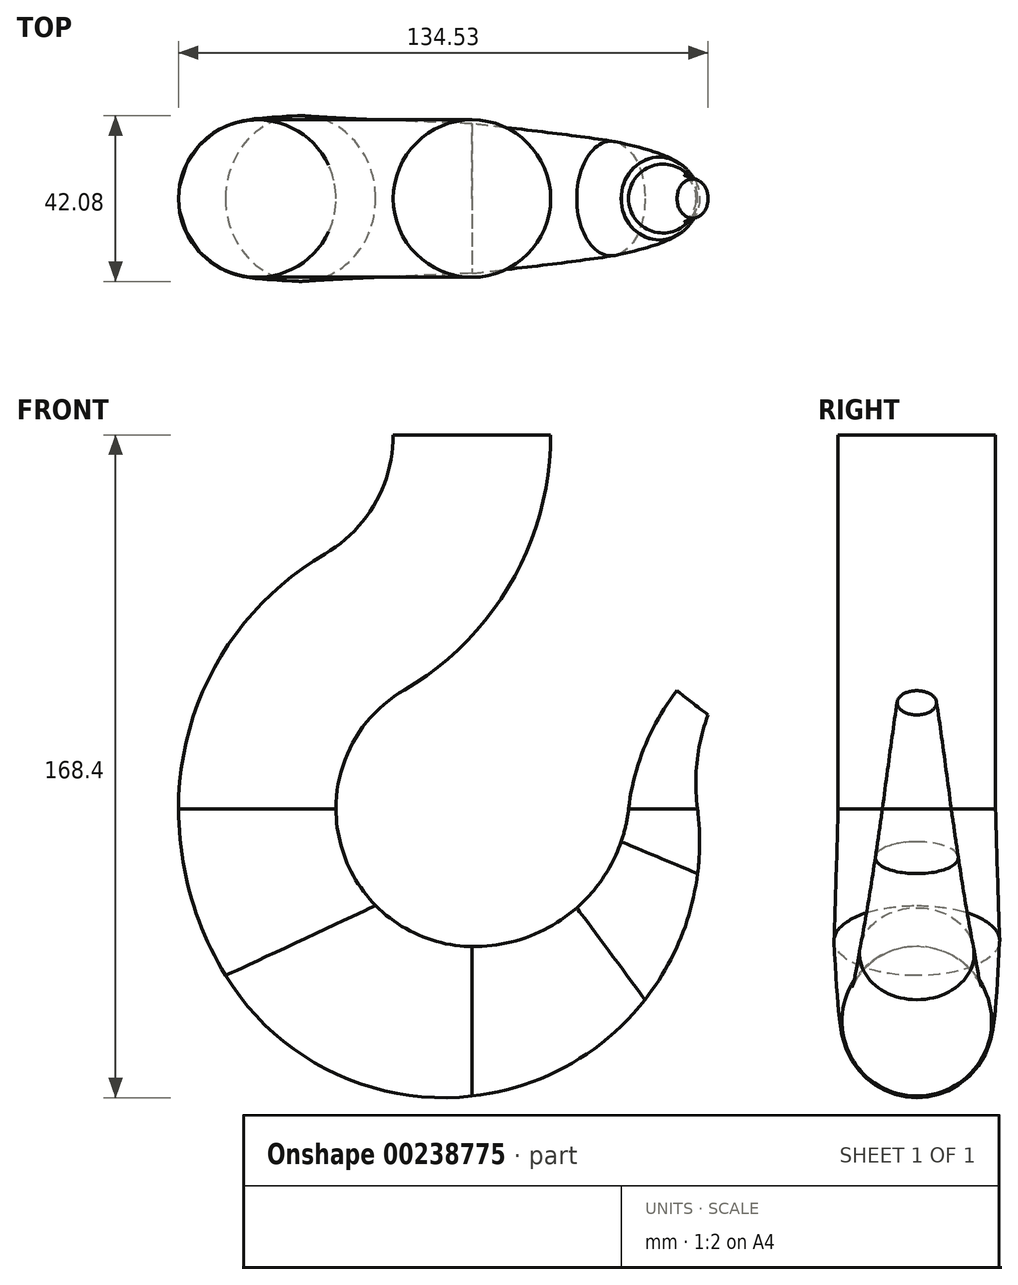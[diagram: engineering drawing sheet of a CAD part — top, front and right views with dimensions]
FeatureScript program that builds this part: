
annotation { "Feature Type Name" : "Feature", "Feature Type Description" : "" }
export const myFeature = defineFeature(function(context is Context, id is Id, definition is map)
    precondition{}
    {
        {
            var Q0;
            Q0=qCreatedBy(makeId("Front.planeOp"),FACE);
            var sketch = newSketch(context, id + "F0", { "sketchPlane" : qUnion([Q0])});
            skLineSegment(sketch, "E0", {"start": v(-107.33, 0) * mm, "end": v(104.55, 0) * mm, "construction": true});
            skLineSegment(sketch, "E1", {"start": v(-0.45, 95.64) * mm, "end": v(-0.45, -96.04) * mm, "construction": true});
            skLineSegment(sketch, "E2", {"start": v(-20.45, 95) * mm, "end": v(19.55, 95) * mm});
            skPoint(sketch, "E3", {"position": v(-0.45, 95) * mm});
            skArc(sketch, "E4", {"start": v(-37.8, 64.77) * mm, "mid": v(-25.1, 77.57) * mm, "end": v(-20.45, 95) * mm});
            skArc(sketch, "E5", {"start": v(-37.8, 64.77) * mm, "mid": v(-65.04, 37.35) * mm, "end": v(-75, 0) * mm});
            skArc(sketch, "E6", {"start": v(-0.45, -73) * mm, "mid": v(43.5, -48.52) * mm, "end": v(56.83, 0) * mm});
            skArc(sketch, "E7", {"start": v(-35, 0) * mm, "mid": v(-24.9, -24.59) * mm, "end": v(-0.45, -35) * mm});
            skArc(sketch, "E8", {"start": v(19.55, 95) * mm, "mid": v(9.59, 57.65) * mm, "end": v(-17.64, 30.23) * mm});
            skArc(sketch, "E9", {"start": v(-35, 0) * mm, "mid": v(-30.35, 17.43) * mm, "end": v(-17.64, 30.23) * mm});
            skArc(sketch, "E10", {"start": v(-0.45, -35) * mm, "mid": v(26.18, -25.15) * mm, "end": v(39.35, 0) * mm});
            skLineSegment(sketch, "E11", {"start": v(32.25, 30) * mm, "end": v(90.74, 30) * mm, "construction": true});
            skPoint(sketch, "E12", {"position": v(67.18, 30) * mm});
            skLineSegment(sketch, "E13", {"start": v(47.43, 30) * mm, "end": v(67.18, 30) * mm});
            skArc(sketch, "E14", {"start": v(-75, 0) * mm, "mid": v(-71.95, -22.02) * mm, "end": v(-63.04, -42.38) * mm});
            skArc(sketch, "E15", {"start": v(39.35, 0) * mm, "mid": v(43.43, 15.85) * mm, "end": v(51.64, 30) * mm});
            skLineSegment(sketch, "E16", {"start": v(51.64, 30) * mm, "end": v(59.53, 23.85) * mm});
            skCircle(sketch, "E17", {"center": v(55.59, 26.92) * mm, "radius": 5 * mm, "construction": true});
            skArc(sketch, "E18", {"start": v(56.83, 0) * mm, "mid": v(56.72, 12.09) * mm, "end": v(59.53, 23.85) * mm});
            skArc(sketch, "E19", {"start": v(-63.04, -42.38) * mm, "mid": v(-36.2, -66.78) * mm, "end": v(-0.45, -73) * mm});
            skLineSegment(sketch, "E20", {"start": v(-37.8, 64.77) * mm, "end": v(-17.64, 30.23) * mm});
            skLineSegment(sketch, "E21", {"start": v(-75, 0) * mm, "end": v(-35, 0) * mm});
            skLineSegment(sketch, "E22", {"start": v(-0.45, -35) * mm, "end": v(-0.45, -73) * mm});
            skLineSegment(sketch, "E23", {"start": v(39.35, 0) * mm, "end": v(56.83, 0) * mm});
            skLineSegment(sketch, "E24", {"start": v(-24.9, -24.59) * mm, "end": v(-63.04, -42.38) * mm});
            skLineSegment(sketch, "E25", {"start": v(26.18, -25.15) * mm, "end": v(43.5, -48.52) * mm});
            skLineSegment(sketch, "E26", {"start": v(37.44, -8.37) * mm, "end": v(56.87, -16.47) * mm});
            skPoint(sketch, "E27", {"position": v(-0.45, 0) * mm});
            skSolve(sketch);
        }
        {
            var Q0;
            Q0=qCreatedBy(makeId("Top.planeOp"),FACE);
            cPlane(context, id + "F1", {"entities" : qUnion([Q0]), "cplaneType" : CPlaneType.OFFSET, "offset" : 95 * mm, "width" : 150 * mm, "height" : 150 * mm});
        }
        {
            var Q0;
            Q0=qCreatedBy(id+"F1.planeOp",FACE);
            var sketch = newSketch(context, id + "F2", { "sketchPlane" : qUnion([Q0])});
            skPoint(sketch, "E28.0", {"position": v(-20.45, 0) * mm});
            skPoint(sketch, "E29.0", {"position": v(-0.45, 0) * mm});
            skCircle(sketch, "E30", {"center": v(-0.45, 0) * mm, "radius": 20 * mm});
            skSolve(sketch);
        }
        {
            var Q0;
            Q0=sQuery(id+"F0.wireOp",EDGE,"E20");
            cPlane(context, id + "F3", {"entities" : qUnion([Q0]), "cplaneType" : CPlaneType.LINE_ANGLE, "offset" : 25 * mm, "angle" : 0 * degree, "width" : 150 * mm, "height" : 150 * mm});
        }
        {
            var Q0;
            Q0=qCreatedBy(id+"F3.planeOp",FACE);
            var sketch = newSketch(context, id + "F4", { "sketchPlane" : qUnion([Q0])});
            skPoint(sketch, "E31.0", {"position": v(0, 75) * mm});
            skPoint(sketch, "E32.0", {"position": v(0, 55) * mm});
            skCircle(sketch, "E33", {"center": v(0, 55) * mm, "radius": 20 * mm});
            skSolve(sketch);
        }
        {
            var Q0;
            Q0=sQuery(id+"F0.wireOp",EDGE,"E21");
            cPlane(context, id + "F5", {"entities" : qUnion([Q0]), "cplaneType" : CPlaneType.LINE_ANGLE, "offset" : 25 * mm, "angle" : 90 * degree, "width" : 150 * mm, "height" : 150 * mm});
        }
        {
            var Q0;
            Q0=qCreatedBy(id+"F5.planeOp",FACE);
            var sketch = newSketch(context, id + "F6", { "sketchPlane" : qUnion([Q0])});
            skPoint(sketch, "E34.0", {"position": v(-55, 0) * mm});
            skPoint(sketch, "E35.0", {"position": v(-75, 0) * mm});
            skCircle(sketch, "E36", {"center": v(-55, 0) * mm, "radius": 20 * mm});
            skSolve(sketch);
        }
        {
            var Q0;
            Q0=makeQuery(id+"F4.imprint","IMPRINT",FACE,{"disambiguationData":[TD([[makeQuery(id+"F4.imprint","IMPRINT",EDGE,{"derivedFrom":sQuery(id+"F4.wireOp",EDGE,"E33")}),1.0]])]});
            var Q1;
            Q1=makeQuery(id+"F6.imprint","IMPRINT",FACE,{"disambiguationData":[TD([[makeQuery(id+"F6.imprint","IMPRINT",EDGE,{"derivedFrom":sQuery(id+"F6.wireOp",EDGE,"E36")}),1.0]])]});
            var Q2;
            Q2=sQuery(id+"F0.wireOp",EDGE,"E5");
            var Q3;
            Q3=sQuery(id+"F0.wireOp",EDGE,"E9");
            loft(context, id + "F7", {"addGuides" : true, "sheetProfilesArray" : [{ "sheetProfileEntities" : qUnion([Q0]) }, { "sheetProfileEntities" : qUnion([Q1]) }], "guidesArray" : [{ "guideEntities" : qUnion([Q2]), "guideDerivativeType" : LoftGuideDerivativeType.DEFAULT, "guideDerivativeMagnitude" : 1 }, { "guideEntities" : qUnion([Q3]), "guideDerivativeType" : LoftGuideDerivativeType.DEFAULT, "guideDerivativeMagnitude" : 1 }]});
        }
        {
            var Q1;
            Q1=makeQuery(id+"F7.opLoft","CAP_FACE",FACE,{"disambiguationData":[OSD([makeQuery(id+"F4.imprint","IMPRINT",FACE,{"disambiguationData":[TD([[makeQuery(id+"F4.imprint","IMPRINT",EDGE,{"derivedFrom":sQuery(id+"F4.wireOp",EDGE,"E33")}),1.0]])]})])],"isStart":true});
            var Q2;
            Q2=makeQuery(id+"F2.imprint","IMPRINT",FACE,{"disambiguationData":[TD([[makeQuery(id+"F2.imprint","IMPRINT",EDGE,{"derivedFrom":sQuery(id+"F2.wireOp",EDGE,"E30")}),1.0]])]});
            var Q3;
            Q3=sQuery(id+"F0.wireOp",EDGE,"E4");
            var Q4;
            Q4=sQuery(id+"F0.wireOp",EDGE,"E8");
            loft(context, id + "F8", {"operationType" : NewBodyOperationType.ADD, "addGuides" : true, "sheetProfilesArray" : [{ "sheetProfileEntities" : qUnion([Q1]) }, { "sheetProfileEntities" : qUnion([Q2]) }], "guidesArray" : [{ "guideEntities" : qUnion([Q3]), "guideDerivativeType" : LoftGuideDerivativeType.DEFAULT, "guideDerivativeMagnitude" : 1 }, { "guideEntities" : qUnion([Q4]), "guideDerivativeType" : LoftGuideDerivativeType.DEFAULT, "guideDerivativeMagnitude" : 1 }]});
        }
        {
            var Q0;
            Q0=sQuery(id+"F0.wireOp",EDGE,"E23");
            cPlane(context, id + "F9", {"entities" : qUnion([Q0]), "cplaneType" : CPlaneType.LINE_ANGLE, "offset" : 25 * mm, "angle" : 90 * degree, "width" : 150 * mm, "height" : 150 * mm});
        }
        {
            var Q0;
            Q0=qCreatedBy(id+"F9.planeOp",FACE);
            var sketch = newSketch(context, id + "F10", { "sketchPlane" : qUnion([Q0])});
            skPoint(sketch, "E37.0", {"position": v(48.09, 0) * mm});
            skPoint(sketch, "E38.0", {"position": v(56.83, 0) * mm});
            skCircle(sketch, "E39", {"center": v(48.09, 0) * mm, "radius": 8.74 * mm});
            skSolve(sketch);
        }
        {
            var Q0;
            Q0=sQuery(id+"F0.wireOp",EDGE,"E16");
            cPlane(context, id + "F11", {"entities" : qUnion([Q0]), "cplaneType" : CPlaneType.LINE_ANGLE, "offset" : 25 * mm, "angle" : 90 * degree, "width" : 150 * mm, "height" : 150 * mm});
        }
        {
            var Q0;
            Q0=qCreatedBy(id+"F11.planeOp",FACE);
            var sketch = newSketch(context, id + "F12", { "sketchPlane" : qUnion([Q0])});
            skLineSegment(sketch, "E40.0", {"start": v(22.27, 0) * mm, "end": v(32.27, 0) * mm, "construction": true});
            skCircle(sketch, "E41", {"center": v(27.27, 0) * mm, "radius": 5 * mm});
            skSolve(sketch);
        }
        {
            var Q0;
            Q0=makeQuery(id+"F0.imprint","IMPRINT",FACE,{"disambiguationData":[TD([[makeQuery(id+"F0.imprint","IMPRINT",EDGE,{"derivedFrom":sQuery(id+"F0.wireOp",EDGE,"E14")}),1.0]])]});
            var sketch = newSketch(context, id + "F13", { "sketchPlane" : qUnion([Q0])});
            skLineSegment(sketch, "E42.0.0", {"start": v(-63.04, -42.38) * mm, "end": v(-24.9, -24.59) * mm});
            skArc(sketch, "E42.0.1", {"start": v(-24.9, -24.59) * mm, "mid": v(-32.38, -13.29) * mm, "end": v(-35, 0) * mm});
            skLineSegment(sketch, "E42.0.2", {"start": v(-35, 0) * mm, "end": v(-75, 0) * mm});
            skArc(sketch, "E42.0.3", {"start": v(-75, 0) * mm, "mid": v(-71.95, -22.02) * mm, "end": v(-63.04, -42.38) * mm});
            skSolve(sketch);
        }
        {
            var Q0;
            Q0=makeQuery(id+"F0.imprint","IMPRINT",FACE,{"disambiguationData":[TD([[makeQuery(id+"F0.imprint","IMPRINT",EDGE,{"derivedFrom":sQuery(id+"F0.wireOp",EDGE,"E19")}),1.0]])]});
            var sketch = newSketch(context, id + "F14", { "sketchPlane" : qUnion([Q0])});
            skArc(sketch, "E43.0.0", {"start": v(-0.45, -35) * mm, "mid": v(-13.7, -32.2) * mm, "end": v(-24.9, -24.59) * mm});
            skLineSegment(sketch, "E43.0.1", {"start": v(-24.9, -24.59) * mm, "end": v(-63.04, -42.38) * mm});
            skArc(sketch, "E43.0.2", {"start": v(-63.04, -42.38) * mm, "mid": v(-36.2, -66.78) * mm, "end": v(-0.45, -73) * mm});
            skLineSegment(sketch, "E43.0.3", {"start": v(-0.45, -73) * mm, "end": v(-0.45, -35) * mm});
            skSolve(sketch);
        }
        {
            var Q0;
            Q0=sQuery(id+"F14.wireOp",EDGE,"E43.0.1");
            cPlane(context, id + "F15", {"entities" : qUnion([Q0]), "cplaneType" : CPlaneType.LINE_ANGLE, "offset" : 25 * mm, "angle" : 90 * degree, "width" : 150 * mm, "height" : 150 * mm});
        }
        {
            var Q0;
            Q0=qCreatedBy(id+"F15.planeOp",FACE);
            var sketch = newSketch(context, id + "F16", { "sketchPlane" : qUnion([Q0])});
            skPoint(sketch, "E44.0", {"position": v(-54, 0) * mm});
            skPoint(sketch, "E45.0", {"position": v(-75.05, 0) * mm});
            skCircle(sketch, "E46", {"center": v(-54, 0) * mm, "radius": 21.04 * mm});
            skSolve(sketch);
        }
        {
            var Q0;
            Q0=makeQuery(id+"F7.opLoft","CAP_FACE",FACE,{"disambiguationData":[OSD([makeQuery(id+"F6.imprint","IMPRINT",FACE,{"disambiguationData":[TD([[makeQuery(id+"F6.imprint","IMPRINT",EDGE,{"derivedFrom":sQuery(id+"F6.wireOp",EDGE,"E36")}),1.0]])]})])],"isStart":true});
            var Q1;
            Q1=makeQuery(id+"F16.imprint","IMPRINT",FACE,{"disambiguationData":[TD([[makeQuery(id+"F16.imprint","IMPRINT",EDGE,{"derivedFrom":sQuery(id+"F16.wireOp",EDGE,"E46")}),1.0]])]});
            var Q2;
            Q2=sQuery(id+"F13.wireOp",EDGE,"E42.0.3");
            var Q3;
            Q3=sQuery(id+"F13.wireOp",EDGE,"E42.0.1");
            loft(context, id + "F17", {"addGuides" : true, "sheetProfilesArray" : [{ "sheetProfileEntities" : qUnion([Q0]) }, { "sheetProfileEntities" : qUnion([Q1]) }], "guidesArray" : [{ "guideEntities" : qUnion([Q2]), "guideDerivativeType" : LoftGuideDerivativeType.DEFAULT, "guideDerivativeMagnitude" : 1 }, { "guideEntities" : qUnion([Q3]), "guideDerivativeType" : LoftGuideDerivativeType.DEFAULT, "guideDerivativeMagnitude" : 1 }]});
        }
        {
            var Q0;
            Q0=sQuery(id+"F14.wireOp",EDGE,"E43.0.3");
            cPlane(context, id + "F18", {"entities" : qUnion([Q0]), "cplaneType" : CPlaneType.LINE_ANGLE, "offset" : 25 * mm, "angle" : 0 * degree, "width" : 150 * mm, "height" : 150 * mm});
        }
        {
            var Q0;
            Q0=qCreatedBy(id+"F18.planeOp",FACE);
            var sketch = newSketch(context, id + "F19", { "sketchPlane" : qUnion([Q0])});
            skPoint(sketch, "E47.0", {"position": v(0, -73) * mm});
            skPoint(sketch, "E48.0", {"position": v(0, -54) * mm});
            skCircle(sketch, "E49", {"center": v(0, -54) * mm, "radius": 19 * mm});
            skSolve(sketch);
        }
        {
            var Q1;
            Q1=makeQuery(id+"F17.opLoft","CAP_FACE",FACE,{"disambiguationData":[OSD([makeQuery(id+"F16.imprint","IMPRINT",FACE,{"disambiguationData":[TD([[makeQuery(id+"F16.imprint","IMPRINT",EDGE,{"derivedFrom":sQuery(id+"F16.wireOp",EDGE,"E46")}),1.0]])]})])],"isStart":true});
            var Q2;
            Q2=makeQuery(id+"F19.imprint","IMPRINT",FACE,{"disambiguationData":[TD([[makeQuery(id+"F19.imprint","IMPRINT",EDGE,{"derivedFrom":sQuery(id+"F19.wireOp",EDGE,"E49")}),1.0]])]});
            var Q3;
            Q3=sQuery(id+"F14.wireOp",EDGE,"E43.0.2");
            var Q4;
            Q4=sQuery(id+"F14.wireOp",EDGE,"E43.0.0");
            loft(context, id + "F20", {"operationType" : NewBodyOperationType.ADD, "addGuides" : true, "sheetProfilesArray" : [{ "sheetProfileEntities" : qUnion([Q1]) }, { "sheetProfileEntities" : qUnion([Q2]) }], "guidesArray" : [{ "guideEntities" : qUnion([Q3]), "guideDerivativeType" : LoftGuideDerivativeType.DEFAULT, "guideDerivativeMagnitude" : 1 }, { "guideEntities" : qUnion([Q4]), "guideDerivativeType" : LoftGuideDerivativeType.DEFAULT, "guideDerivativeMagnitude" : 1 }]});
        }
        {
            var Q0;
            Q0=sQuery(id+"F0.wireOp",EDGE,"E25");
            cPlane(context, id + "F21", {"entities" : qUnion([Q0]), "cplaneType" : CPlaneType.LINE_ANGLE, "offset" : 25 * mm, "angle" : 0 * degree, "width" : 150 * mm, "height" : 150 * mm});
        }
        {
            var Q0;
            Q0=qCreatedBy(id+"F21.planeOp",FACE);
            var sketch = newSketch(context, id + "F22", { "sketchPlane" : qUnion([Q0])});
            skPoint(sketch, "E50.0", {"position": v(0, -50.34) * mm});
            skPoint(sketch, "E51.0", {"position": v(0, -35.8) * mm});
            skCircle(sketch, "E52", {"center": v(0, -50.34) * mm, "radius": 14.55 * mm});
            skSolve(sketch);
        }
        {
            var Q0;
            {var subQ0=sQuery(id+"F0.wireOp",EDGE,"E22");Q0=makeQuery(id+"F0.imprint","IMPRINT",FACE,{"disambiguationData":[TD([[makeQuery(id+"F0.imprint","IMPRINT",EDGE,{"derivedFrom":subQ0}),1.0]])]});}
            var sketch = newSketch(context, id + "F23", { "sketchPlane" : qUnion([Q0])});
            skLineSegment(sketch, "E53.0.0", {"start": v(43.5, -48.52) * mm, "end": v(26.18, -25.15) * mm});
            skArc(sketch, "E53.0.1", {"start": v(26.18, -25.15) * mm, "mid": v(13.78, -32.55) * mm, "end": v(-0.45, -35) * mm});
            skLineSegment(sketch, "E53.0.2", {"start": v(-0.45, -35) * mm, "end": v(-0.45, -73) * mm});
            skArc(sketch, "E53.0.3", {"start": v(-0.45, -73) * mm, "mid": v(24, -65.19) * mm, "end": v(43.5, -48.52) * mm});
            skSolve(sketch);
        }
        {
            var Q0;
            Q0=makeQuery(id+"F20.opLoft","CAP_FACE",FACE,{"disambiguationData":[OSD([makeQuery(id+"F19.imprint","IMPRINT",FACE,{"disambiguationData":[TD([[makeQuery(id+"F19.imprint","IMPRINT",EDGE,{"derivedFrom":sQuery(id+"F19.wireOp",EDGE,"E49")}),1.0]])]})])],"isStart":true});
            var Q1;
            Q1=makeQuery(id+"F22.imprint","IMPRINT",FACE,{"disambiguationData":[TD([[makeQuery(id+"F22.imprint","IMPRINT",EDGE,{"derivedFrom":sQuery(id+"F22.wireOp",EDGE,"E52")}),1.0]])]});
            var Q2;
            Q2=sQuery(id+"F23.wireOp",EDGE,"E53.0.3");
            var Q3;
            Q3=sQuery(id+"F23.wireOp",EDGE,"E53.0.1");
            loft(context, id + "F24", {"addGuides" : true, "sheetProfilesArray" : [{ "sheetProfileEntities" : qUnion([Q0]) }, { "sheetProfileEntities" : qUnion([Q1]) }], "guidesArray" : [{ "guideEntities" : qUnion([Q2]), "guideDerivativeType" : LoftGuideDerivativeType.DEFAULT, "guideDerivativeMagnitude" : 1 }, { "guideEntities" : qUnion([Q3]), "guideDerivativeType" : LoftGuideDerivativeType.DEFAULT, "guideDerivativeMagnitude" : 1 }]});
        }
        {
            var Q0;
            Q0=sQuery(id+"F0.wireOp",EDGE,"E26");
            cPlane(context, id + "F25", {"entities" : qUnion([Q0]), "cplaneType" : CPlaneType.LINE_ANGLE, "offset" : 25 * mm, "angle" : 90 * degree, "width" : 150 * mm, "height" : 150 * mm});
        }
        {
            var Q0;
            Q0=qCreatedBy(id+"F25.planeOp",FACE);
            var sketch = newSketch(context, id + "F26", { "sketchPlane" : qUnion([Q0])});
            skPoint(sketch, "E54.0", {"position": v(48.3, 0) * mm});
            skPoint(sketch, "E55.0", {"position": v(37.78, 0) * mm});
            skCircle(sketch, "E56", {"center": v(48.3, 0) * mm, "radius": 10.52 * mm});
            skSolve(sketch);
        }
        {
            var Q0;
            {var subQ0=sQuery(id+"F0.wireOp",EDGE,"E25");Q0=makeQuery(id+"F0.imprint","IMPRINT",FACE,{"disambiguationData":[TD([[makeQuery(id+"F0.imprint","IMPRINT",EDGE,{"derivedFrom":subQ0}),1.0]])]});}
            var sketch = newSketch(context, id + "F27", { "sketchPlane" : qUnion([Q0])});
            skLineSegment(sketch, "E57.0.0", {"start": v(56.87, -16.47) * mm, "end": v(37.44, -8.37) * mm});
            skArc(sketch, "E57.0.1", {"start": v(37.44, -8.37) * mm, "mid": v(32.9, -17.5) * mm, "end": v(26.18, -25.15) * mm});
            skLineSegment(sketch, "E57.0.2", {"start": v(26.18, -25.15) * mm, "end": v(43.5, -48.52) * mm});
            skArc(sketch, "E57.0.3", {"start": v(43.5, -48.52) * mm, "mid": v(52.37, -33.4) * mm, "end": v(56.87, -16.47) * mm});
            skSolve(sketch);
        }
        {
            var Q1;
            Q1=makeQuery(id+"F26.imprint","IMPRINT",FACE,{"disambiguationData":[TD([[makeQuery(id+"F26.imprint","IMPRINT",EDGE,{"derivedFrom":sQuery(id+"F26.wireOp",EDGE,"E56")}),1.0]])]});
            var Q2;
            Q2=makeQuery(id+"F24.opLoft","CAP_FACE",FACE,{"disambiguationData":[OSD([makeQuery(id+"F22.imprint","IMPRINT",FACE,{"disambiguationData":[TD([[makeQuery(id+"F22.imprint","IMPRINT",EDGE,{"derivedFrom":sQuery(id+"F22.wireOp",EDGE,"E52")}),1.0]])]})])],"isStart":true});
            var Q3;
            Q3=sQuery(id+"F27.wireOp",EDGE,"E57.0.1");
            var Q4;
            Q4=sQuery(id+"F27.wireOp",EDGE,"E57.0.3");
            loft(context, id + "F28", {"operationType" : NewBodyOperationType.ADD, "addGuides" : true, "sheetProfilesArray" : [{ "sheetProfileEntities" : qUnion([Q1]) }, { "sheetProfileEntities" : qUnion([Q2]) }], "guidesArray" : [{ "guideEntities" : qUnion([Q3]), "guideDerivativeType" : LoftGuideDerivativeType.DEFAULT, "guideDerivativeMagnitude" : 1 }, { "guideEntities" : qUnion([Q4]), "guideDerivativeType" : LoftGuideDerivativeType.DEFAULT, "guideDerivativeMagnitude" : 1 }]});
        }
        {
            var Q0;
            {var subQ0=sQuery(id+"F0.wireOp",EDGE,"E23");Q0=makeQuery(id+"F0.imprint","IMPRINT",FACE,{"disambiguationData":[TD([[makeQuery(id+"F0.imprint","IMPRINT",EDGE,{"derivedFrom":subQ0}),-1.0]])]});}
            var sketch = newSketch(context, id + "F29", { "sketchPlane" : qUnion([Q0])});
            skArc(sketch, "E58.0.0", {"start": v(39.35, 0) * mm, "mid": v(38.62, -4.24) * mm, "end": v(37.44, -8.37) * mm});
            skLineSegment(sketch, "E58.0.1", {"start": v(37.44, -8.37) * mm, "end": v(56.87, -16.47) * mm});
            skArc(sketch, "E58.0.2", {"start": v(56.87, -16.47) * mm, "mid": v(57.37, -8.23) * mm, "end": v(56.83, 0) * mm});
            skLineSegment(sketch, "E58.0.3", {"start": v(56.83, 0) * mm, "end": v(39.35, 0) * mm});
            skSolve(sketch);
        }
        {
            var Q0;
            Q0=makeQuery(id+"F10.imprint","IMPRINT",FACE,{"disambiguationData":[TD([[makeQuery(id+"F10.imprint","IMPRINT",EDGE,{"derivedFrom":sQuery(id+"F10.wireOp",EDGE,"E39")}),1.0]])]});
            var Q1;
            Q1=makeQuery(id+"F28.opLoft","CAP_FACE",FACE,{"disambiguationData":[OSD([makeQuery(id+"F26.imprint","IMPRINT",FACE,{"disambiguationData":[TD([[makeQuery(id+"F26.imprint","IMPRINT",EDGE,{"derivedFrom":sQuery(id+"F26.wireOp",EDGE,"E56")}),1.0]])]})])],"isStart":true});
            var Q2;
            Q2=sQuery(id+"F29.wireOp",EDGE,"E58.0.0");
            var Q3;
            Q3=sQuery(id+"F29.wireOp",EDGE,"E58.0.2");
            loft(context, id + "F30", {"addGuides" : true, "sheetProfilesArray" : [{ "sheetProfileEntities" : qUnion([Q0]) }, { "sheetProfileEntities" : qUnion([Q1]) }], "guidesArray" : [{ "guideEntities" : qUnion([Q2]), "guideDerivativeType" : LoftGuideDerivativeType.DEFAULT, "guideDerivativeMagnitude" : 1 }, { "guideEntities" : qUnion([Q3]), "guideDerivativeType" : LoftGuideDerivativeType.DEFAULT, "guideDerivativeMagnitude" : 1 }]});
        }
        {
            var Q1;
            Q1=makeQuery(id+"F12.imprint","IMPRINT",FACE,{"disambiguationData":[TD([[makeQuery(id+"F12.imprint","IMPRINT",EDGE,{"derivedFrom":sQuery(id+"F12.wireOp",EDGE,"E41")}),1.0]])]});
            var Q2;
            Q2=makeQuery(id+"F30.opLoft","CAP_FACE",FACE,{"disambiguationData":[OSD([makeQuery(id+"F10.imprint","IMPRINT",FACE,{"disambiguationData":[TD([[makeQuery(id+"F10.imprint","IMPRINT",EDGE,{"derivedFrom":sQuery(id+"F10.wireOp",EDGE,"E39")}),1.0]])]})])],"isStart":true});
            var Q3;
            Q3=sQuery(id+"F0.wireOp",EDGE,"E18");
            var Q4;
            Q4=sQuery(id+"F0.wireOp",EDGE,"E15");
            loft(context, id + "F31", {"operationType" : NewBodyOperationType.ADD, "addGuides" : true, "sheetProfilesArray" : [{ "sheetProfileEntities" : qUnion([Q1]) }, { "sheetProfileEntities" : qUnion([Q2]) }], "guidesArray" : [{ "guideEntities" : qUnion([Q3]), "guideDerivativeType" : LoftGuideDerivativeType.DEFAULT, "guideDerivativeMagnitude" : 1 }, { "guideEntities" : qUnion([Q4]), "guideDerivativeType" : LoftGuideDerivativeType.DEFAULT, "guideDerivativeMagnitude" : 1 }]});
        }
    });
